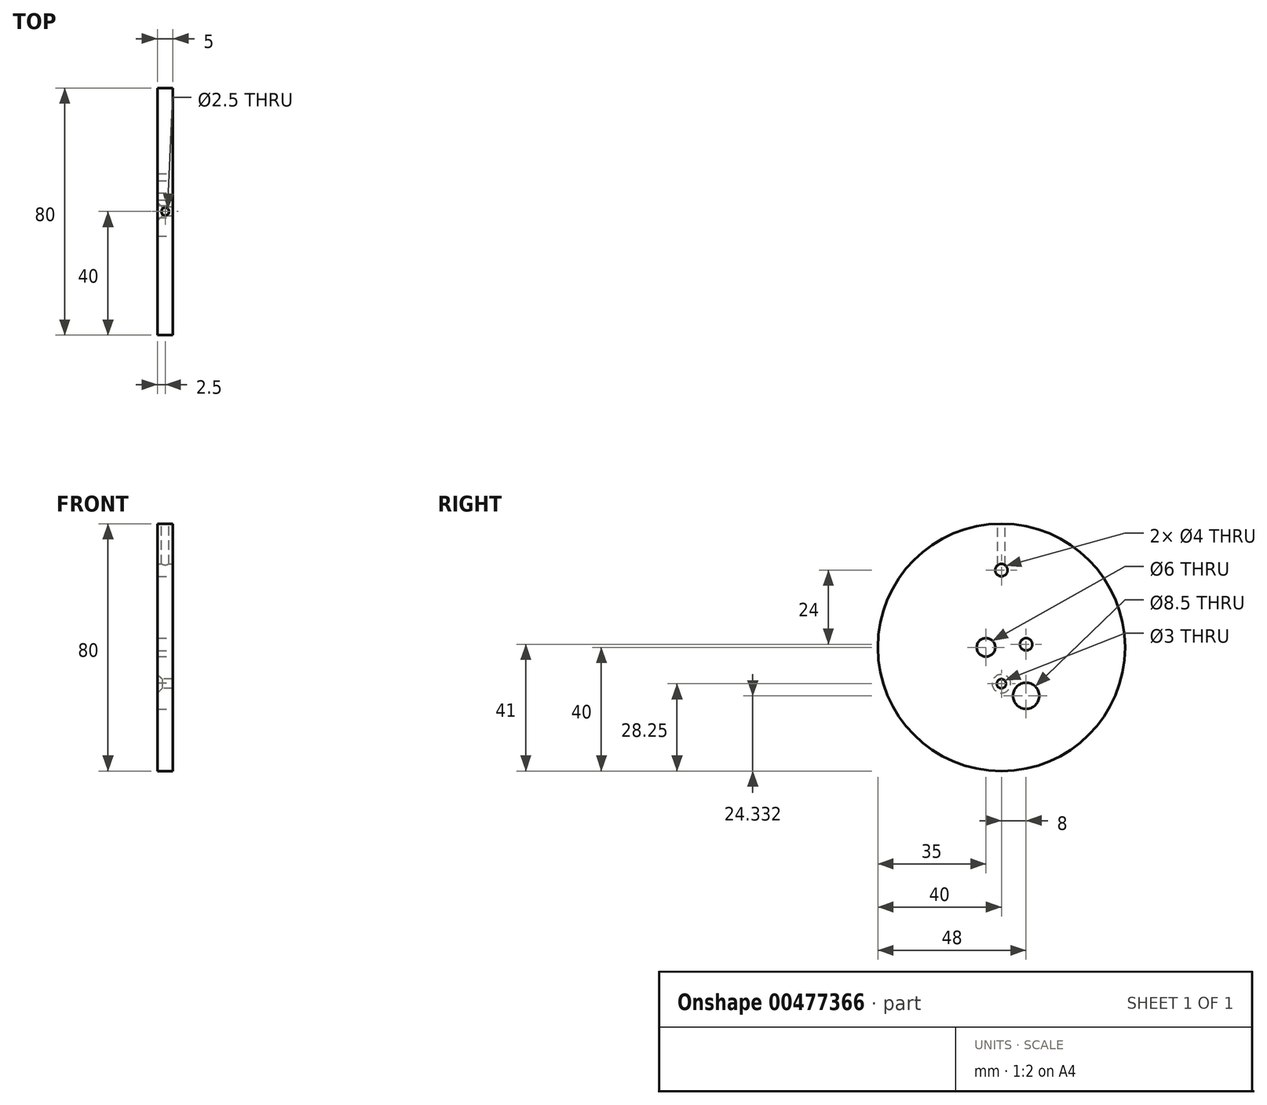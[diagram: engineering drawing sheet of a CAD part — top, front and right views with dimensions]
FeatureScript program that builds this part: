
annotation { "Feature Type Name" : "Feature", "Feature Type Description" : "" }
export const myFeature = defineFeature(function(context is Context, id is Id, definition is map)
    precondition{}
    {
        {
            var Q0;
            Q0=qCreatedBy(makeId("Front.planeOp"),FACE);
            var sketch = newSketch(context, id + "F0", { "sketchPlane" : qUnion([Q0])});
            skLineSegment(sketch, "E0", {"start": v(0, 0) * mm, "end": v(0, 40) * mm});
            skLineSegment(sketch, "E1", {"start": v(0, 40) * mm, "end": v(5, 40) * mm});
            skLineSegment(sketch, "E2", {"start": v(5, 40) * mm, "end": v(5, 0) * mm});
            skLineSegment(sketch, "E3", {"start": v(5, 0) * mm, "end": v(0, 0) * mm});
            skSolve(sketch);
        }
        {
            var Q0;
            Q0=makeQuery(id+"F0.imprint","IMPRINT",FACE,{"disambiguationData":[TD([[makeQuery(id+"F0.imprint","IMPRINT",EDGE,{"derivedFrom":sQuery(id+"F0.wireOp",EDGE,"E0")}),-1.0]])]});
            var Q1;
            Q1=sQuery(id+"F0.wireOp",EDGE,"E3");
            revolve(context, id + "F1", {"entities" : qUnion([Q0]), "axis" : qUnion([Q1]), "revolveType" : RevolveType.FULL});
        }
        {
            var Q0;
            Q0=makeQuery(id+"F1.opRevolve","SWEPT_FACE",FACE,{"disambiguationData":[OSD([sQuery(id+"F0.wireOp",EDGE,"E2")])]});
            var sketch = newSketch(context, id + "F2", { "sketchPlane" : qUnion([Q0])});
            skPoint(sketch, "E4", {"position": v(-5, 0) * mm});
            skPoint(sketch, "E5", {"position": v(8, 1) * mm});
            skPoint(sketch, "E6", {"position": v(8, -15.67) * mm});
            skPoint(sketch, "E7", {"position": v(0, 25) * mm});
            skPoint(sketch, "E8", {"position": v(0, -11.75) * mm});
            skSolve(sketch);
        }
        {
            var Q0;
            Q0=sQuery(id+"F2.wireOp",VERTEX,"E5");
            var Q1;
            Q1=makeQuery(id+"F1.opRevolve","SWEPT_BODY",BODY,{"disambiguationData":[OSD([sQuery(id+"F0.wireOp",EDGE,"E0"),sQuery(id+"F0.wireOp",EDGE,"E1"),sQuery(id+"F0.wireOp",EDGE,"E2"),sQuery(id+"F0.wireOp",EDGE,"E3")])]});
            hole(context, id + "F3", {"style" : HoleStyle.SIMPLE, "endStyle" : HoleEndStyle.THROUGH, "holeDiameter" : 4 * mm, "isTappedThrough" : true, "tappedDepth" : 13.6 * mm, "tapClearance" : 2, "locations" : qUnion([Q0]), "scope" : qUnion([Q1])});
        }
        {
            var Q0;
            Q0=sQuery(id+"F2.wireOp",VERTEX,"E7");
            var Q1;
            Q1=makeQuery(id+"F1.opRevolve","SWEPT_BODY",BODY,{"disambiguationData":[OSD([sQuery(id+"F0.wireOp",EDGE,"E0"),sQuery(id+"F0.wireOp",EDGE,"E1"),sQuery(id+"F0.wireOp",EDGE,"E2"),sQuery(id+"F0.wireOp",EDGE,"E3")])]});
            hole(context, id + "F4", {"style" : HoleStyle.SIMPLE, "endStyle" : HoleEndStyle.THROUGH, "holeDiameter" : 4 * mm, "isTappedThrough" : true, "tappedDepth" : 13.6 * mm, "tapClearance" : 2, "locations" : qUnion([Q0]), "scope" : qUnion([Q1])});
        }
        {
            var Q0;
            Q0=sQuery(id+"F2.wireOp",VERTEX,"E4");
            var Q1;
            Q1=makeQuery(id+"F1.opRevolve","SWEPT_BODY",BODY,{"disambiguationData":[OSD([sQuery(id+"F0.wireOp",EDGE,"E0"),sQuery(id+"F0.wireOp",EDGE,"E1"),sQuery(id+"F0.wireOp",EDGE,"E2"),sQuery(id+"F0.wireOp",EDGE,"E3")])]});
            hole(context, id + "F5", {"style" : HoleStyle.SIMPLE, "endStyle" : HoleEndStyle.THROUGH, "holeDiameter" : 6 * mm, "isTappedThrough" : true, "tappedDepth" : 13.6 * mm, "tapClearance" : 2, "locations" : qUnion([Q0]), "scope" : qUnion([Q1])});
        }
        {
            var Q0;
            Q0=sQuery(id+"F2.wireOp",VERTEX,"E6");
            var Q1;
            Q1=makeQuery(id+"F1.opRevolve","SWEPT_BODY",BODY,{"disambiguationData":[OSD([sQuery(id+"F0.wireOp",EDGE,"E0"),sQuery(id+"F0.wireOp",EDGE,"E1"),sQuery(id+"F0.wireOp",EDGE,"E2"),sQuery(id+"F0.wireOp",EDGE,"E3")])]});
            hole(context, id + "F6", {"style" : HoleStyle.SIMPLE, "endStyle" : HoleEndStyle.THROUGH, "standardTappedOrClearance" : lookupTablePath({ "standard" : "ISO", "engagement" : "75%", "pitch" : "1.5 mm", "size" : "M10", "type" : "Tapped" }), "standardBlindInLast" : lookupTablePath({ "standard" : "ISO", "engagement" : "75%", "pitch" : "1.5 mm", "size" : "M10", "type" : "Tapped" }), "holeDiameter" : 8.5 * mm, "showTappedDepth" : true, "isTappedThrough" : true, "tappedDepth" : 13.6 * mm, "tapClearance" : 2, "locations" : qUnion([Q0]), "scope" : qUnion([Q1]), "majorDiameter" : 10 * mm});
        }
        {
            var Q0;
            Q0=makeQuery(id+"F1.opRevolve","SWEPT_FACE",FACE,{"disambiguationData":[OSD([sQuery(id+"F0.wireOp",EDGE,"E0")])]});
            var sketch = newSketch(context, id + "F7", { "sketchPlane" : qUnion([Q0])});
            skPoint(sketch, "E9", {"position": v(0, -11.75) * mm});
            skSolve(sketch);
        }
        {
            var Q0;
            Q0=sQuery(id+"F7.wireOp",VERTEX,"E9");
            var Q1;
            Q1=makeQuery(id+"F1.opRevolve","SWEPT_BODY",BODY,{"disambiguationData":[OSD([sQuery(id+"F0.wireOp",EDGE,"E0"),sQuery(id+"F0.wireOp",EDGE,"E1"),sQuery(id+"F0.wireOp",EDGE,"E2"),sQuery(id+"F0.wireOp",EDGE,"E3")])]});
            hole(context, id + "F8", {"style" : HoleStyle.C_SINK, "endStyle" : HoleEndStyle.THROUGH, "holeDiameter" : 3 * mm, "cSinkDiameter" : 6 * mm, "cSinkAngle" : 90 * degree, "isTappedThrough" : true, "tappedDepth" : 13.6 * mm, "tapClearance" : 2, "locations" : qUnion([Q0]), "scope" : qUnion([Q1])});
        }
        {
            var Q0;
            Q0=qCreatedBy(makeId("Top.planeOp"),FACE);
            cPlane(context, id + "F9", {"entities" : qUnion([Q0]), "cplaneType" : CPlaneType.OFFSET, "offset" : 40 * mm, "width" : 150 * mm, "height" : 150 * mm});
        }
        {
            var Q0;
            Q0=qCreatedBy(id+"F9.planeOp",FACE);
            var sketch = newSketch(context, id + "F10", { "sketchPlane" : qUnion([Q0])});
            skPoint(sketch, "E10", {"position": v(2.5, 0) * mm});
            skSolve(sketch);
        }
        {
            var Q0;
            Q0=sQuery(id+"F10.wireOp",VERTEX,"E10");
            var Q1;
            Q1=makeQuery(id+"F1.opRevolve","SWEPT_BODY",BODY,{"disambiguationData":[OSD([sQuery(id+"F0.wireOp",EDGE,"E0"),sQuery(id+"F0.wireOp",EDGE,"E1"),sQuery(id+"F0.wireOp",EDGE,"E2"),sQuery(id+"F0.wireOp",EDGE,"E3")])]});
            hole(context, id + "F11", {"style" : HoleStyle.SIMPLE, "endStyle" : HoleEndStyle.BLIND, "standardTappedOrClearance" : lookupTablePath({ "standard" : "ISO", "engagement" : "75%", "pitch" : "0.5 mm", "size" : "M3", "type" : "Tapped" }), "standardBlindInLast" : lookupTablePath({ "standard" : "ISO", "engagement" : "75%", "pitch" : "0.5 mm", "size" : "M3", "type" : "Tapped" }), "holeDiameter" : 2.5 * mm, "showTappedDepth" : true, "holeDepth" : 14.6 * mm, "isTappedThrough" : true, "tappedDepth" : 13.6 * mm, "tapClearance" : 2, "locations" : qUnion([Q0]), "scope" : qUnion([Q1]), "majorDiameter" : 3 * mm});
        }
    });
